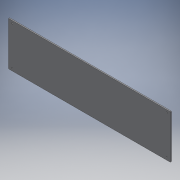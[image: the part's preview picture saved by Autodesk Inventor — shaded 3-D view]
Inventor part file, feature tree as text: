
AUTODESK INVENTOR PART (.ipt)
format: ipt  version: 2019 (Build 230136000, 136)  size: 117,248 bytes
history: native  units: in
note: dims shown in document units (in); Inventor stores cm internally (conversion verified against a paired STEP export)
features: reference x3, other x3, extrude x1, fillet x1, sketch x1, helix x1
ambient origin geometry x8: Origin, YZ Plane, XZ Plane, XY Plane, X Axis, Y Axis, Z Axis, Center Point
bodies: Solid1 (feature_tree)
feature tree (10):
  extrude  "Extrusion1"  Depth=0.0787in
  fillet  "Fillet1"  Radius=0.1969in
  sketch  "Sketch1"  dims[d0=6.6929in d1=0.1969in d2=0.1969in d3=0.1969in d4=0.1969in d5=0.3937in d6=0.3937in d7=0.3937in d8=0.3937in d9=0.1575in d10=0.0in d11=0.0787in]
  reference  "Reference1"
  reference  "Reference2"
  reference  "Reference3"
  other  "<userpath>\Documents\CAD Files\Helix DLP\Helix DLP.iam"
  helix  "Helix DLP.iam"  [1 undecoded]
  other  "30X30 - T-slot - Aluminium Profile_CPY_CPY_CPY_CPY:2"
  other  "30X30 - T-slot - Aluminium Profile_CPY_CPY_CPY_CPY:1"
note: 1 required parameter value undecoded (feature->parameter linkage not recoverable at this tier; creation-order binding heuristic only, values carry confidence <= 0.55)
